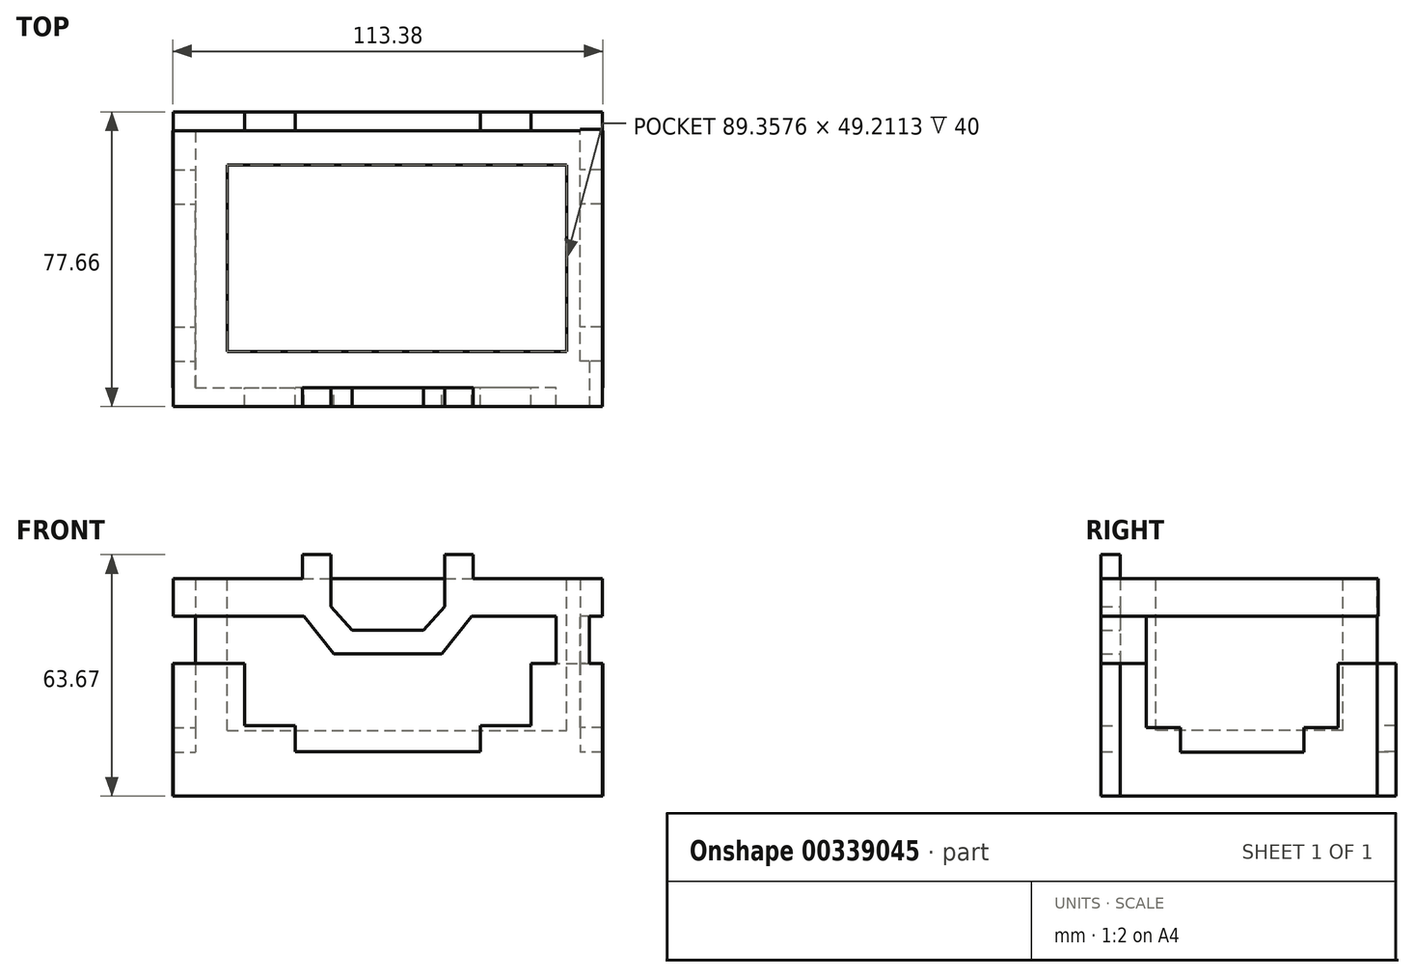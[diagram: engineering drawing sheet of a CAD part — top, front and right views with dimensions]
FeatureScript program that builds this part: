
annotation { "Feature Type Name" : "Feature", "Feature Type Description" : "" }
export const myFeature = defineFeature(function(context is Context, id is Id, definition is map)
    precondition{}
    {
        {
            var Q0;
            Q0=qCreatedBy(makeId("Top.planeOp"),FACE);
            var sketch = newSketch(context, id + "F0", { "sketchPlane" : qUnion([Q0])});
            skLineSegment(sketch, "E0.bottom", {"start": v(-50.69, 35.5) * mm, "end": v(50.69, 35.5) * mm});
            skLineSegment(sketch, "E0.top", {"start": v(-50.69, -32.17) * mm, "end": v(50.69, -32.17) * mm});
            skLineSegment(sketch, "E0.left", {"start": v(-50.69, 35.5) * mm, "end": v(-50.69, -32.17) * mm});
            skLineSegment(sketch, "E0.right", {"start": v(50.69, 35.5) * mm, "end": v(50.69, -32.17) * mm});
            skSolve(sketch);
        }
        {
            var Q0;
            Q0 = qSketchRegion(id + "F0", true);
            extrude(context, id + "F1", {"entities" : qUnion([Q0]), "depth" : 57.3 * mm});
        }
        {
            var Q0;
            Q0=makeQuery(id+"F1.opExtrude","CAP_FACE",FACE,{"disambiguationData":[OSD([sQuery(id+"F0.wireOp",EDGE,"E0.bottom"),sQuery(id+"F0.wireOp",EDGE,"E0.top"),sQuery(id+"F0.wireOp",EDGE,"E0.left"),sQuery(id+"F0.wireOp",EDGE,"E0.right")])],"isStart":false});
            var sketch = newSketch(context, id + "F2", { "sketchPlane" : qUnion([Q0])});
            skLineSegment(sketch, "E1.bottom", {"start": v(-42.3, 26.48) * mm, "end": v(47.06, 26.48) * mm});
            skLineSegment(sketch, "E1.top", {"start": v(-42.3, -22.73) * mm, "end": v(47.06, -22.73) * mm});
            skLineSegment(sketch, "E1.left", {"start": v(-42.3, 26.48) * mm, "end": v(-42.3, -22.73) * mm});
            skLineSegment(sketch, "E1.right", {"start": v(47.06, 26.48) * mm, "end": v(47.06, -22.73) * mm});
            skSolve(sketch);
        }
        {
            var Q0;
            Q0 = qSketchRegion(id + "F2", true);
            extrude(context, id + "F3", {"entities" : qUnion([Q0]), "operationType" : NewBodyOperationType.REMOVE, "oppositeDirection" : true, "depth" : 40 * mm});
        }
        {
            var Q0;
            Q0=makeQuery(id+"F1.opExtrude","SWEPT_FACE",FACE,{"disambiguationData":[OSD([sQuery(id+"F0.wireOp",EDGE,"E0.top")])]});
            var sketch = newSketch(context, id + "F4", { "sketchPlane" : qUnion([Q0])});
            skLineSegment(sketch, "E2", {"start": v(-50.69, 0) * mm, "end": v(-56.5, 0) * mm});
            skLineSegment(sketch, "E3", {"start": v(-56.5, 0) * mm, "end": v(-56.5, 35) * mm});
            skLineSegment(sketch, "E4", {"start": v(-56.5, 35) * mm, "end": v(-37.77, 35) * mm});
            skLineSegment(sketch, "E5", {"start": v(-37.77, 35) * mm, "end": v(-37.77, 18.6) * mm});
            skLineSegment(sketch, "E6", {"start": v(-37.77, 18.6) * mm, "end": v(-24.34, 18.6) * mm});
            skLineSegment(sketch, "E7", {"start": v(-24.34, 18.6) * mm, "end": v(-24.34, 0) * mm});
            skLineSegment(sketch, "E8", {"start": v(0, 11.7) * mm, "end": v(-24.34, 11.7) * mm});
            skLineSegment(sketch, "E9", {"start": v(-50.69, 35) * mm, "end": v(-50.69, 47.47) * mm});
            skLineSegment(sketch, "E10", {"start": v(-50.69, 47.47) * mm, "end": v(-38.03, 47.47) * mm});
            skLineSegment(sketch, "E11", {"start": v(-50.69, 47.47) * mm, "end": v(-56.5, 47.47) * mm});
            skLineSegment(sketch, "E12", {"start": v(-56.5, 47.47) * mm, "end": v(-56.5, 57.3) * mm});
            skLineSegment(sketch, "E13", {"start": v(-56.5, 57.3) * mm, "end": v(-22.52, 57.3) * mm});
            skLineSegment(sketch, "E14", {"start": v(-22.52, 57.3) * mm, "end": v(-22.52, 63.67) * mm});
            skLineSegment(sketch, "E15", {"start": v(-22.52, 63.67) * mm, "end": v(-17.64, 63.67) * mm});
            skLineSegment(sketch, "E16", {"start": v(-17.64, 63.67) * mm, "end": v(-14.97, 63.67) * mm});
            skLineSegment(sketch, "E17", {"start": v(-38.03, 47.47) * mm, "end": v(-22.09, 47.47) * mm});
            skLineSegment(sketch, "E18", {"start": v(-22.09, 47.47) * mm, "end": v(-14.24, 37.49) * mm});
            skLineSegment(sketch, "E19", {"start": v(-14.24, 37.49) * mm, "end": v(0, 37.49) * mm});
            skLineSegment(sketch, "E20", {"start": v(-14.97, 63.67) * mm, "end": v(-14.97, 49.91) * mm});
            skLineSegment(sketch, "E21", {"start": v(-14.97, 49.91) * mm, "end": v(-9.43, 43.7) * mm});
            skLineSegment(sketch, "E22", {"start": v(-9.43, 43.7) * mm, "end": v(0, 43.7) * mm});
            skLineSegment(sketch, "E23", {"start": v(-44.36, 47.47) * mm, "end": v(-44.36, 35) * mm});
            skLineSegment(sketch, "E24.MirrorCS", {"start": v(14.24, 37.49) * mm, "end": v(0, 37.49) * mm});
            skLineSegment(sketch, "E25.MirrorCS", {"start": v(9.43, 43.7) * mm, "end": v(0, 43.7) * mm});
            skLineSegment(sketch, "E26.MirrorCS", {"start": v(14.97, 49.91) * mm, "end": v(9.43, 43.7) * mm});
            skLineSegment(sketch, "E27.MirrorCS", {"start": v(22.09, 47.47) * mm, "end": v(14.24, 37.49) * mm});
            skLineSegment(sketch, "E28.MirrorCS", {"start": v(14.97, 63.67) * mm, "end": v(14.97, 49.91) * mm});
            skLineSegment(sketch, "E29.MirrorCS", {"start": v(0, 11.7) * mm, "end": v(24.34, 11.7) * mm});
            skLineSegment(sketch, "E30.MirrorCS", {"start": v(24.34, 18.6) * mm, "end": v(24.34, 0) * mm});
            skLineSegment(sketch, "E31.MirrorCS", {"start": v(37.77, 18.6) * mm, "end": v(24.34, 18.6) * mm});
            skLineSegment(sketch, "E32.MirrorCS", {"start": v(37.77, 35) * mm, "end": v(37.77, 18.6) * mm});
            skLineSegment(sketch, "E33.MirrorCS", {"start": v(56.5, 47.47) * mm, "end": v(56.5, 57.3) * mm});
            skLineSegment(sketch, "E34.MirrorCS", {"start": v(50.69, 47.47) * mm, "end": v(56.5, 47.47) * mm});
            skLineSegment(sketch, "E35.MirrorCS", {"start": v(50.69, 47.47) * mm, "end": v(38.03, 47.47) * mm});
            skLineSegment(sketch, "E36.MirrorCS", {"start": v(17.64, 63.67) * mm, "end": v(14.97, 63.67) * mm});
            skLineSegment(sketch, "E37.MirrorCS", {"start": v(22.52, 63.67) * mm, "end": v(17.64, 63.67) * mm});
            skLineSegment(sketch, "E38.MirrorCS", {"start": v(22.52, 57.3) * mm, "end": v(22.52, 63.67) * mm});
            skLineSegment(sketch, "E39.MirrorCS", {"start": v(56.5, 0) * mm, "end": v(56.5, 35) * mm});
            skLineSegment(sketch, "E40.MirrorCS", {"start": v(56.5, 35) * mm, "end": v(37.77, 35) * mm});
            skLineSegment(sketch, "E41.MirrorCS", {"start": v(50.69, 0) * mm, "end": v(56.5, 0) * mm});
            skLineSegment(sketch, "E42.MirrorCS", {"start": v(51.37, 34.94) * mm, "end": v(51.37, 47.42) * mm});
            skLineSegment(sketch, "E43.MirrorCS", {"start": v(44.36, 47.47) * mm, "end": v(44.36, 35) * mm});
            skLineSegment(sketch, "E44.MirrorCS", {"start": v(56.5, 57.3) * mm, "end": v(22.52, 57.3) * mm});
            skLineSegment(sketch, "E45.MirrorCS", {"start": v(38.03, 47.47) * mm, "end": v(22.09, 47.47) * mm});
            skLineSegment(sketch, "E46", {"start": v(-50.69, 0) * mm, "end": v(50.69, 0) * mm});
            skLineSegment(sketch, "E47", {"start": v(-50.69, 47.47) * mm, "end": v(-50.69, 35) * mm});
            skLineSegment(sketch, "E48", {"start": v(-50.69, 47.47) * mm, "end": v(-44.36, 47.47) * mm});
            skLineSegment(sketch, "E49", {"start": v(-44.36, 35) * mm, "end": v(-50.69, 35) * mm});
            skSolve(sketch);
        }
        {
            var Q0;
            {var subQ13=sQuery(id+"F4.wireOp",EDGE,"E17");Q0=makeQuery(id+"F4.imprint","IMPRINT",FACE,{"disambiguationData":[TD([[makeQuery(id+"F4.imprint","IMPRINT",EDGE,{"derivedFrom":subQ13}),1.0]])]});}
            extrude(context, id + "F5", {"entities" : qUnion([Q0]), "operationType" : NewBodyOperationType.ADD, "depth" : 5 * mm});
        }
        {
            var Q0;
            {var subQ0=sQuery(id+"F4.wireOp",EDGE,"E11");Q0=makeQuery(id+"F4.imprint","IMPRINT",FACE,{"disambiguationData":[TD([[makeQuery(id+"F4.imprint","IMPRINT",EDGE,{"derivedFrom":subQ0}),-1.0]])]});}
            var Q1;
            {var subQ3=sQuery(id+"F4.wireOp",EDGE,"E33.MirrorCS");Q1=makeQuery(id+"F4.imprint","IMPRINT",FACE,{"disambiguationData":[TD([[makeQuery(id+"F4.imprint","IMPRINT",EDGE,{"derivedFrom":subQ3}),1.0]])]});}
            extrude(context, id + "F6", {"entities" : qUnion([Q0, Q1]), "operationType" : NewBodyOperationType.ADD, "depth" : 5 * mm});
        }
        {
            var Q0;
            {var subQ0=sQuery(id+"F4.wireOp",EDGE,"E43.MirrorCS");Q0=makeQuery(id+"F4.imprint","IMPRINT",FACE,{"disambiguationData":[TD([[makeQuery(id+"F4.imprint","IMPRINT",EDGE,{"derivedFrom":subQ0}),1.0]])]});}
            extrude(context, id + "F7", {"entities" : qUnion([Q0]), "operationType" : NewBodyOperationType.ADD, "depth" : 5 * mm});
        }
        {
            var Q0;
            {var subQ8=sQuery(id+"F4.wireOp",EDGE,"E5");Q0=makeQuery(id+"F4.imprint","IMPRINT",FACE,{"disambiguationData":[TD([[makeQuery(id+"F4.imprint","IMPRINT",EDGE,{"derivedFrom":subQ8}),-1.0]])]});}
            var Q1;
            {var subQ0=sQuery(id+"F4.wireOp",EDGE,"E2");Q1=makeQuery(id+"F4.imprint","IMPRINT",FACE,{"disambiguationData":[TD([[makeQuery(id+"F4.imprint","IMPRINT",EDGE,{"derivedFrom":subQ0}),-1.0]])]});}
            extrude(context, id + "F8", {"entities" : qUnion([Q0, Q1]), "operationType" : NewBodyOperationType.ADD, "depth" : 5 * mm});
        }
        {
            var Q0;
            {var subQ1=sQuery(id+"F4.wireOp",EDGE,"E31.MirrorCS");Q0=makeQuery(id+"F4.imprint","IMPRINT",FACE,{"disambiguationData":[TD([[makeQuery(id+"F4.imprint","IMPRINT",EDGE,{"derivedFrom":subQ1}),1.0]])]});}
            var Q1;
            {var subQ4=sQuery(id+"F4.wireOp",EDGE,"E39.MirrorCS");Q1=makeQuery(id+"F4.imprint","IMPRINT",FACE,{"disambiguationData":[TD([[makeQuery(id+"F4.imprint","IMPRINT",EDGE,{"derivedFrom":subQ4}),1.0]])]});}
            extrude(context, id + "F9", {"entities" : qUnion([Q0, Q1]), "operationType" : NewBodyOperationType.ADD, "depth" : 5 * mm});
        }
        {
            var Q0;
            {var subQ4=sQuery(id+"F4.wireOp",EDGE,"E8");Q0=makeQuery(id+"F4.imprint","IMPRINT",FACE,{"disambiguationData":[TD([[makeQuery(id+"F4.imprint","IMPRINT",EDGE,{"derivedFrom":subQ4}),1.0]])]});}
            extrude(context, id + "F10", {"entities" : qUnion([Q0]), "operationType" : NewBodyOperationType.ADD, "depth" : 5 * mm});
        }
        {
            var Q0;
            {var subQ1=sQuery(id+"F4.wireOp",EDGE,"E36.MirrorCS");Q0=makeQuery(id+"F4.imprint","IMPRINT",FACE,{"disambiguationData":[TD([[makeQuery(id+"F4.imprint","IMPRINT",EDGE,{"derivedFrom":subQ1}),1.0]])]});}
            var Q1;
            {var subQ4=sQuery(id+"F4.wireOp",EDGE,"E14");Q1=makeQuery(id+"F4.imprint","IMPRINT",FACE,{"disambiguationData":[TD([[makeQuery(id+"F4.imprint","IMPRINT",EDGE,{"derivedFrom":subQ4}),-1.0]])]});}
            extrude(context, id + "F11", {"entities" : qUnion([Q0, Q1]), "operationType" : NewBodyOperationType.ADD, "depth" : 5 * mm});
        }
        {
            var Q0;
            {var subQ0=sQuery(id+"F4.wireOp",EDGE,"E48");var subQ1=sQuery(id+"F4.wireOp",EDGE,"E49");var subQ2=sQuery(id+"F4.wireOp",EDGE,"E28.MirrorCS");var subQ3=sQuery(id+"F0.wireOp",EDGE,"E0.top");var subQ4=sQuery(id+"F4.wireOp",EDGE,"E20");var subQ5=sQuery(id+"F4.wireOp",EDGE,"E46");var subQ6=sQuery(id+"F4.wireOp",EDGE,"E30.MirrorCS");var subQ7=sQuery(id+"F4.wireOp",EDGE,"E7");var subQ8=sQuery(id+"F4.wireOp",EDGE,"E40.MirrorCS");var subQ9=sQuery(id+"F4.wireOp",EDGE,"E35.MirrorCS");var subQ10=sQuery(id+"F0.wireOp",EDGE,"E0.right");var subQ11=sQuery(id+"F4.wireOp",EDGE,"E44.MirrorCS");var subQ12=sQuery(id+"F4.wireOp",EDGE,"E13");var subQ13=sQuery(id+"F0.wireOp",EDGE,"E0.left");Q0=makeQuery(id+"F890GEA9djG2osC_1.boolean.opBoolean","MERGE",FACE,{"derivedFrom":[makeQuery(id+"F11.boolean.opBoolean","MERGE",FACE,{"derivedFrom":[makeQuery(id+"F10.boolean.opBoolean","MERGE",FACE,{"derivedFrom":[makeQuery(id+"F8.opExtrude","CAP_FACE",FACE,{"disambiguationData":[OSD([sQuery(id+"F4.wireOp",EDGE,"E2"),sQuery(id+"F4.wireOp",EDGE,"E3"),sQuery(id+"F4.wireOp",EDGE,"E4"),sQuery(id+"F4.wireOp",EDGE,"E5"),sQuery(id+"F4.wireOp",EDGE,"E6"),subQ7,subQ5,subQ1])],"isStart":false}),makeQuery(id+"F9.boolean.opBoolean","MERGE",FACE,{"derivedFrom":[makeQuery(id+"F7.boolean.opBoolean","MERGE",FACE,{"derivedFrom":[makeQuery(id+"F6.boolean.opBoolean","MERGE",FACE,{"derivedFrom":[makeQuery(id+"F5.opExtrude","CAP_FACE",FACE,{"disambiguationData":[OSD([subQ3,subQ13,subQ10,sQuery(id+"F4.wireOp",EDGE,"E10"),subQ12,sQuery(id+"F4.wireOp",EDGE,"E17"),sQuery(id+"F4.wireOp",EDGE,"E18"),sQuery(id+"F4.wireOp",EDGE,"E19"),subQ4,sQuery(id+"F4.wireOp",EDGE,"E21"),sQuery(id+"F4.wireOp",EDGE,"E22"),sQuery(id+"F4.wireOp",EDGE,"E24.MirrorCS"),sQuery(id+"F4.wireOp",EDGE,"E27.MirrorCS"),subQ9,sQuery(id+"F4.wireOp",EDGE,"E26.MirrorCS"),sQuery(id+"F4.wireOp",EDGE,"E25.MirrorCS"),subQ11,subQ2,sQuery(id+"F4.wireOp",EDGE,"E45.MirrorCS"),subQ0])],"isStart":false}),makeQuery(id+"F6.opExtrude","CAP_FACE",FACE,{"disambiguationData":[OSD([subQ3,subQ13,sQuery(id+"F4.wireOp",EDGE,"E11"),sQuery(id+"F4.wireOp",EDGE,"E12"),subQ12])],"isStart":false}),makeQuery(id+"F6.opExtrude","CAP_FACE",FACE,{"disambiguationData":[OSD([subQ3,subQ10,sQuery(id+"F4.wireOp",EDGE,"E33.MirrorCS"),sQuery(id+"F4.wireOp",EDGE,"E34.MirrorCS"),subQ9,subQ11])],"isStart":false})]}),makeQuery(id+"F7.opExtrude","CAP_FACE",FACE,{"disambiguationData":[OSD([subQ3,subQ10,subQ9,subQ8,sQuery(id+"F4.wireOp",EDGE,"E43.MirrorCS")])],"isStart":false})]}),makeQuery(id+"F9.opExtrude","CAP_FACE",FACE,{"disambiguationData":[OSD([subQ6,sQuery(id+"F4.wireOp",EDGE,"E31.MirrorCS"),sQuery(id+"F4.wireOp",EDGE,"E32.MirrorCS"),sQuery(id+"F4.wireOp",EDGE,"E39.MirrorCS"),subQ8,sQuery(id+"F4.wireOp",EDGE,"E41.MirrorCS"),subQ5])],"isStart":false})]}),makeQuery(id+"F10.opExtrude","CAP_FACE",FACE,{"disambiguationData":[OSD([subQ7,sQuery(id+"F4.wireOp",EDGE,"E8"),sQuery(id+"F4.wireOp",EDGE,"E29.MirrorCS"),subQ6,subQ5])],"isStart":false})]}),makeQuery(id+"F11.opExtrude","CAP_FACE",FACE,{"disambiguationData":[OSD([subQ3,sQuery(id+"F4.wireOp",EDGE,"E14"),sQuery(id+"F4.wireOp",EDGE,"E15"),sQuery(id+"F4.wireOp",EDGE,"E16"),subQ4])],"isStart":false}),makeQuery(id+"F11.opExtrude","CAP_FACE",FACE,{"disambiguationData":[OSD([subQ3,sQuery(id+"F4.wireOp",EDGE,"E36.MirrorCS"),sQuery(id+"F4.wireOp",EDGE,"E37.MirrorCS"),subQ2,sQuery(id+"F4.wireOp",EDGE,"E38.MirrorCS")])],"isStart":false})]}),makeQuery(id+"F890GEA9djG2osC_1.opExtrude","CAP_FACE",FACE,{"disambiguationData":[OSD([sQuery(id+"F4.wireOp",EDGE,"E47"),subQ1,sQuery(id+"F4.wireOp",EDGE,"E23"),subQ0])],"isStart":false})]});}
            var sketch = newSketch(context, id + "F12", { "sketchPlane" : qUnion([Q0])});
            skCircle(sketch, "E50", {"center": v(-45.12, 11.15) * mm, "radius": 4.27 * mm});
            skLineSegment(sketch, "E51", {"start": v(0, -21.58) * mm, "end": v(0, 71.53) * mm});
            skPoint(sketch, "E51.startSnap0", {"position": v(0, 11.7) * mm});
            skCircle(sketch, "E52.MirrorC", {"center": v(45.12, 11.15) * mm, "radius": 4.27 * mm});
            skSolve(sketch);
        }
        {
            var Q0;
            {var subQ0=sQuery(id+"F0.wireOp",EDGE,"E0.right");var subQ1=sQuery(id+"F0.wireOp",EDGE,"E0.top");Q0=makeQuery(id+"F7.boolean.opBoolean","MERGE",FACE,{"derivedFrom":[makeQuery(id+"F5.boolean.opBoolean","MERGE",FACE,{"derivedFrom":[makeQuery(id+"F1.opExtrude","SWEPT_FACE",FACE,{"disambiguationData":[OSD([subQ0])]}),makeQuery(id+"F5.opExtrude","SWEPT_FACE",FACE,{"disambiguationData":[OSD([subQ1,subQ0])]})]}),makeQuery(id+"F7.opExtrude","SWEPT_FACE",FACE,{"disambiguationData":[OSD([subQ1,subQ0])]})]});}
            var sketch = newSketch(context, id + "F13", { "sketchPlane" : qUnion([Q0])});
            skSolve(sketch);
        }
        {
            var Q0;
            Q0 = qSketchRegion(id + "F13", true);
            var Q1;
            {var subQ3=sQuery(id+"F4.wireOp",EDGE,"E33.MirrorCS");Q1=makeQuery(id+"F4.imprint","IMPRINT",FACE,{"disambiguationData":[TD([[makeQuery(id+"F4.imprint","IMPRINT",EDGE,{"derivedFrom":subQ3}),1.0]])]});}
            extrude(context, id + "F14", {"entities" : qUnion([Q0, Q1]), "oppositeDirection" : true, "depth" : 5 * mm});
        }
        {
            var Q0;
            Q0=makeQuery(id+"F14.opExtrude","CAP_FACE",FACE,{"disambiguationData":[OSD([sQuery(id+"F0.wireOp",EDGE,"E0.top"),sQuery(id+"F0.wireOp",EDGE,"E0.right"),sQuery(id+"F4.wireOp",EDGE,"E33.MirrorCS"),sQuery(id+"F4.wireOp",EDGE,"E34.MirrorCS"),sQuery(id+"F4.wireOp",EDGE,"E35.MirrorCS"),sQuery(id+"F4.wireOp",EDGE,"E44.MirrorCS")])],"isStart":false});
            extrude(context, id + "F15", {"entities" : qUnion([Q0]), "depth" : 62.6 * mm});
        }
        {
            var Q0;
            Q0=makeQuery(id+"F1.opExtrude","SWEPT_FACE",FACE,{"disambiguationData":[OSD([sQuery(id+"F0.wireOp",EDGE,"E0.bottom")])]});
            var sketch = newSketch(context, id + "F16", { "sketchPlane" : qUnion([Q0])});
            skLineSegment(sketch, "E53.0.0", {"start": v(56.5, 0) * mm, "end": v(0, 0) * mm});
            skLineSegment(sketch, "E53.0.1", {"start": v(0, 0) * mm, "end": v(0, 11.7) * mm});
            skLineSegment(sketch, "E53.0.2", {"start": v(0, 11.7) * mm, "end": v(24.34, 11.7) * mm});
            skLineSegment(sketch, "E53.0.3", {"start": v(24.34, 11.7) * mm, "end": v(24.34, 18.6) * mm});
            skLineSegment(sketch, "E53.0.4", {"start": v(24.34, 18.6) * mm, "end": v(37.77, 18.6) * mm});
            skLineSegment(sketch, "E53.0.5", {"start": v(37.77, 18.6) * mm, "end": v(37.77, 35) * mm});
            skLineSegment(sketch, "E53.0.6", {"start": v(37.77, 35) * mm, "end": v(56.5, 35) * mm});
            skLineSegment(sketch, "E53.0.7", {"start": v(56.5, 35) * mm, "end": v(56.5, 0) * mm});
            skLineSegment(sketch, "E54", {"start": v(0, 57.3) * mm, "end": v(0, 0) * mm});
            skLineSegment(sketch, "E55.MirrorCS", {"start": v(0, 11.7) * mm, "end": v(-24.34, 11.7) * mm});
            skLineSegment(sketch, "E56.MirrorCS", {"start": v(-24.34, 18.6) * mm, "end": v(-37.77, 18.6) * mm});
            skLineSegment(sketch, "E57.MirrorCS", {"start": v(-24.34, 11.7) * mm, "end": v(-24.34, 18.6) * mm});
            skLineSegment(sketch, "E58.MirrorCS", {"start": v(-37.77, 18.6) * mm, "end": v(-37.77, 35) * mm});
            skLineSegment(sketch, "E59.MirrorCS", {"start": v(-37.77, 35) * mm, "end": v(-56.5, 35) * mm});
            skLineSegment(sketch, "E60.MirrorCS", {"start": v(-56.5, 35) * mm, "end": v(-56.5, 0) * mm});
            skLineSegment(sketch, "E61.MirrorCS", {"start": v(-56.5, 0) * mm, "end": v(0, 0) * mm});
            skSolve(sketch);
        }
        {
            var Q0;
            {var subQ0=sQuery(id+"F16.wireOp",EDGE,"E53.0.1");Q0=makeQuery(id+"F16.imprint","IMPRINT",FACE,{"disambiguationData":[TD([[makeQuery(id+"F16.imprint","IMPRINT",EDGE,{"derivedFrom":subQ0}),1.0]])]});}
            var Q1;
            {var subQ0=sQuery(id+"F16.wireOp",EDGE,"E53.0.2");Q1=makeQuery(id+"F16.imprint","IMPRINT",FACE,{"disambiguationData":[TD([[makeQuery(id+"F16.imprint","IMPRINT",EDGE,{"derivedFrom":subQ0}),-1.0]])]});}
            var Q2;
            {var subQ0=sQuery(id+"F16.wireOp",EDGE,"E60.MirrorCS");Q2=makeQuery(id+"F16.imprint","IMPRINT",FACE,{"disambiguationData":[TD([[makeQuery(id+"F16.imprint","IMPRINT",EDGE,{"derivedFrom":subQ0}),1.0]])]});}
            var Q3;
            {var subQ3=sQuery(id+"F16.wireOp",EDGE,"E53.0.7");Q3=makeQuery(id+"F16.imprint","IMPRINT",FACE,{"disambiguationData":[TD([[makeQuery(id+"F16.imprint","IMPRINT",EDGE,{"derivedFrom":subQ3}),-1.0]])]});}
            extrude(context, id + "F17", {"entities" : qUnion([Q0, Q1, Q2, Q3]), "operationType" : NewBodyOperationType.ADD, "depth" : 5 * mm});
        }
        {
            var Q0;
            {var subQ0=sQuery(id+"F0.wireOp",EDGE,"E0.left");Q0=makeQuery(id+"F5.boolean.opBoolean","MERGE",FACE,{"derivedFrom":[makeQuery(id+"F1.opExtrude","SWEPT_FACE",FACE,{"disambiguationData":[OSD([subQ0])]}),makeQuery(id+"F5.opExtrude","SWEPT_FACE",FACE,{"disambiguationData":[OSD([sQuery(id+"F0.wireOp",EDGE,"E0.top"),subQ0])]})]});}
            var sketch = newSketch(context, id + "F18", { "sketchPlane" : qUnion([Q0])});
            skLineSegment(sketch, "E62", {"start": v(-35.5, 35) * mm, "end": v(-25.25, 35) * mm});
            skLineSegment(sketch, "E63", {"start": v(-25.25, 35) * mm, "end": v(-25.25, 18.13) * mm});
            skLineSegment(sketch, "E64", {"start": v(-25.25, 18.13) * mm, "end": v(-16.24, 18.13) * mm});
            skLineSegment(sketch, "E65", {"start": v(-16.24, 18.13) * mm, "end": v(-16.24, 11.57) * mm});
            skLineSegment(sketch, "E66", {"start": v(-16.24, 11.57) * mm, "end": v(0, 11.57) * mm});
            skLineSegment(sketch, "E67.MirrorCS", {"start": v(35.5, 35) * mm, "end": v(25.25, 35) * mm});
            skLineSegment(sketch, "E68.MirrorCS", {"start": v(25.25, 35) * mm, "end": v(25.25, 18.13) * mm});
            skLineSegment(sketch, "E69.MirrorCS", {"start": v(25.25, 18.13) * mm, "end": v(16.24, 18.13) * mm});
            skLineSegment(sketch, "E70.MirrorCS", {"start": v(16.24, 18.13) * mm, "end": v(16.24, 11.57) * mm});
            skLineSegment(sketch, "E71.MirrorCS", {"start": v(16.24, 11.57) * mm, "end": v(0, 11.57) * mm});
            skSolve(sketch);
        }
        {
            var Q0;
            Q0 = qSketchRegion(id + "F18", true);
            var Q1;
            Q1=makeQuery(id+"F18.imprint","IMPRINT",FACE,{"disambiguationData":[TD([[makeQuery(id+"F18.imprint","IMPRINT",EDGE,{"derivedFrom":sQuery(id+"F18.wireOp",EDGE,"E62")}),-1.0]])]});
            extrude(context, id + "F19", {"entities" : qUnion([Q0, Q1]), "operationType" : NewBodyOperationType.ADD, "depth" : 6 * mm});
        }
        {
            var Q0;
            {var subQ0=sQuery(id+"F0.wireOp",EDGE,"E0.right");Q0=makeQuery(id+"F13.imprint","IMPRINT",FACE,{"disambiguationData":[TD([[makeQuery(id+"F13.imprint","IMPRINT",EDGE,{"derivedFrom":makeQuery(id+"F1.opExtrude","CAP_EDGE",EDGE,{"disambiguationData":[OSD([subQ0])],"isStart":true})}),-1.0]])]});}
            var sketch = newSketch(context, id + "F20", { "sketchPlane" : qUnion([Q0])});
            skLineSegment(sketch, "E72.0.0", {"start": v(-32.17, 0) * mm, "end": v(-32.17, 35) * mm});
            skLineSegment(sketch, "E72.0.1", {"start": v(-32.17, 35) * mm, "end": v(-25.25, 35) * mm});
            skLineSegment(sketch, "E72.0.2", {"start": v(-25.25, 35) * mm, "end": v(-25.25, 18.13) * mm});
            skLineSegment(sketch, "E72.0.3", {"start": v(-25.25, 18.13) * mm, "end": v(-16.24, 18.13) * mm});
            skLineSegment(sketch, "E72.0.4", {"start": v(-16.24, 18.13) * mm, "end": v(-16.24, 11.57) * mm});
            skLineSegment(sketch, "E72.0.5", {"start": v(-16.24, 11.57) * mm, "end": v(16.24, 11.57) * mm});
            skLineSegment(sketch, "E72.0.6", {"start": v(16.24, 11.57) * mm, "end": v(16.24, 18.13) * mm});
            skLineSegment(sketch, "E72.0.7", {"start": v(16.24, 18.13) * mm, "end": v(25.25, 18.13) * mm});
            skLineSegment(sketch, "E72.0.8", {"start": v(25.25, 18.13) * mm, "end": v(25.25, 35) * mm});
            skLineSegment(sketch, "E72.0.9", {"start": v(25.25, 35) * mm, "end": v(35.5, 35) * mm});
            skLineSegment(sketch, "E72.0.10", {"start": v(35.5, 35) * mm, "end": v(35.5, 0) * mm});
            skLineSegment(sketch, "E72.0.11", {"start": v(35.5, 0) * mm, "end": v(-32.17, 0) * mm});
            skSolve(sketch);
        }
        {
            var Q0;
            Q0=makeQuery(id+"F20.imprint","IMPRINT",FACE,{"disambiguationData":[TD([[makeQuery(id+"F20.imprint","IMPRINT",EDGE,{"derivedFrom":sQuery(id+"F20.wireOp",EDGE,"E72.0.0")}),1.0]])]});
            extrude(context, id + "F21", {"entities" : qUnion([Q0]), "operationType" : NewBodyOperationType.ADD, "depth" : 6 * mm});
        }
        {
            var Q0;
            {var subQ0=sQuery(id+"F4.wireOp",EDGE,"E11");Q0=makeQuery(id+"F4.imprint","IMPRINT",FACE,{"disambiguationData":[TD([[makeQuery(id+"F4.imprint","IMPRINT",EDGE,{"derivedFrom":subQ0}),-1.0]])]});}
            extrude(context, id + "F22", {"entities" : qUnion([Q0]), "operationType" : NewBodyOperationType.ADD, "oppositeDirection" : true, "depth" : 67.6 * mm});
        }
        {
            var Q0;
            {var subQ6=sQuery(id+"F4.wireOp",EDGE,"E33.MirrorCS");Q0=makeQuery(id+"F4.imprint","IMPRINT",FACE,{"disambiguationData":[TD([[makeQuery(id+"F4.imprint","IMPRINT",EDGE,{"derivedFrom":subQ6}),1.0]])]});}
            extrude(context, id + "F23", {"entities" : qUnion([Q0]), "operationType" : NewBodyOperationType.ADD, "oppositeDirection" : true, "depth" : 68 * mm});
        }
        {
            var Q0;
            {var subQ0=sQuery(id+"F0.wireOp",EDGE,"E0.right");Q0=makeQuery(id+"F13.imprint","IMPRINT",FACE,{"disambiguationData":[TD([[makeQuery(id+"F13.imprint","IMPRINT",EDGE,{"derivedFrom":makeQuery(id+"F1.opExtrude","CAP_EDGE",EDGE,{"disambiguationData":[OSD([subQ0])],"isStart":true})}),-1.0]])]});}
            var sketch = newSketch(context, id + "F24", { "sketchPlane" : qUnion([Q0])});
            skLineSegment(sketch, "E73", {"start": v(-37.17, 47.69) * mm, "end": v(-37.17, 34.99) * mm});
            skLineSegment(sketch, "E74", {"start": v(-37.17, 34.99) * mm, "end": v(-32.28, 34.99) * mm});
            skLineSegment(sketch, "E75", {"start": v(-32.28, 34.99) * mm, "end": v(-25.26, 34.99) * mm});
            skLineSegment(sketch, "E76", {"start": v(-25.26, 34.99) * mm, "end": v(-25.26, 47.61) * mm});
            skLineSegment(sketch, "E77", {"start": v(-25.26, 47.61) * mm, "end": v(-37.17, 47.69) * mm});
            skSolve(sketch);
        }
        {
            var Q0;
            Q0 = qSketchRegion(id + "F24", true);
            extrude(context, id + "F25", {"entities" : qUnion([Q0]), "operationType" : NewBodyOperationType.ADD, "depth" : 2.4 * mm});
        }
    });
